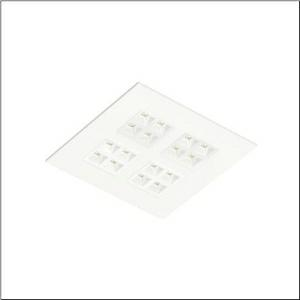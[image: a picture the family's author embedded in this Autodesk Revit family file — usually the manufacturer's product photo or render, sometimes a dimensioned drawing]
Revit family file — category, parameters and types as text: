
# Revit family: silica_31_square_51my6ndu44wa
name_source: partatom
category: Lighting Fixtures
units: mm (PartAtom-declared; Revit-internal decimal feet)

## family parameters
Cut with Voids When Loaded = No
Host = Face
Light Source = No
Part Type = Normal
Room Calculation Point = No
Round Connector Dimension = Use Diameter
Shared = No

## types (1)
- --- (1 x LED, 6640 lm, 38.5 W, 4000K)
    Apparent Load = 39 VA
    CIE Flux Codes = 81 99 100 100 100
    Color Rendering = 80
    Color Temperature = 4000K
    Default Elevation = 1800 mm
    Description = Silica 31 Square, office luminaire, primary light control with lens, of PMMA, primary anti-glare with reflector, of PC, white, light emission: direct distribution, primary light characteristic: symmetric, installation type: lay-in mounting, LED, rated luminous flux: 4.570lm, luminous efficacy: 176lm/W, light colour: 840, colour temperature: 4000K, control gear: DALI 2, Multilumen, with terminal, 5-pole, mains connection: 220..240V, AC, 50/60Hz, rated input power: 26W, luminaire housing, of sheet steel, coated, traffic white (RAL 9016), module: M625, length: 620mm, width: 620mm, height: 43mm, protection rating (complete): IP20, insulation class (complete): insulation class II (safety insulation), certification: CE, impact resistance: IK03, permissible operating ambient temperature: -20..+35°C, standard: EN 50419, packaging unit: 1 piece
    Height = 0 mm  [stored 0 ft]
    Lamp = 1 x LED
    Lamp Light Flux = 6640 lm
    Lamp Power = 38.5 W
    Lamp count = 1
    Length = 620 mm
    Luminous efficacy = 172 lm/W
    Manufacturer = Siteco
    ModVariant = No
    Model = 51MY6NDU44WA
    Mounting Place = Ceiling
    Mounting Type = Recessed
    Number of Poles = 1
    OnlyDefault = Yes
    Power Factor = 1
    Product Name = Silica 31 Square
    Product group = office luminaire | ceiling recessed
    ProductGroupID = 400
    Protection Class = Protection class II
    Protection Degree = IP 20
    RLX_Detail_Level = 1
    RLX_Emergency_Light_Flux = 0 lm
    RLX_Emergency_Type = 0
    RLX_Emergency_Type_DB = No
    RlxData = <blob elided: 28233 chars, md5=b4a3dfba>
    Socket = socket
    Standby Power = 0 W
    System Light Flux = 6640 lm
    System Power = 39 W
    Type Comments = factory setting: luminous flux: 100 % | (OFF | OFF | OFF | OFF) | 1050 mA
    Type Image = l_1313651.jpg
    URL = http://relux.com
    VarID = @adj_043137
    Voltage = 0 V
    Weight = 0.00 kg
    Width = 620 mm

note: [stored X ft] marks values corroborated as IEEE doubles in the binary element streams (Revit-internal decimal feet)

## geometry (parser evidence)
native form markers: Blend x4, Sweep x9
no freeform markers — native parametric forms only
